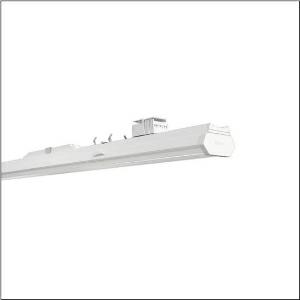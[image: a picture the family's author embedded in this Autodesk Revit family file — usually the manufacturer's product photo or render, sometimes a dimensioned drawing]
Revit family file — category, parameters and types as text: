
# Revit family: licross_r__11_protected_extreme_mo_51tp12dn495ge_fe34
name_source: partatom
category: Lighting Fixtures
units: mm (PartAtom-declared; Revit-internal decimal feet)

## family parameters
Cut with Voids When Loaded = No
Host = Face
Light Source = No
Part Type = Normal
Room Calculation Point = No
Round Connector Dimension = Use Diameter
Shared = No

## types (1)
- --- (1 x LED, 9980 lm, 57.1 W, 4000K)
    Apparent Load = 57 VA
    CIE Flux Codes = 73 92 98 99 100
    Color Rendering = 80
    Color Temperature = 4000K
    Default Elevation = 1800 mm
    Description = Licross® 11 Protected extreme MO, luminaire insert, of sheet steel, galvanised, coil coated, white, length: 1.500mm, width: 90mm, height: 101mm, LED rated luminous flux: 9.980lm, light colour: 840, control gear: DALI 2, with plug, 5-pole, with phase selection, mains connection: 220..240V, AC, 50/60Hz, rated input power: 57W, halogen-free wiring, primary optical cover: cover, of PMMA, light emission: direct distribution, primary light characteristic: symmetric, protection rating (complete): IP64, insulation class (complete): insulation class I (protective earthing), certification: CE, ENEC, VDE, UKCA, protection symbol: D if used in an environment with conductive dust loads with corresponding accessories, impact resistance: IK06, permissible ambient temperature for indoor applications: -40..+45°C, corresponds to IFS (International Featured Standards) requirements for safety and quality in the food industry, reducing of maximum allowable ambient temperature of 5°C with ceiling mounting, LABS conformity tested according to VDMA 24364:2018-05, packaging unit: 1 piece
    Height = 92 mm
    Lamp = 1 x LED
    Lamp Light Flux = 9980 lm
    Lamp Power = 57.1 W
    Lamp count = 1
    Length = 1500 mm
    Luminous efficacy = 175 lm/W
    Manufacturer = Siteco
    ModVariant = No
    Model = 51TP12DN495GE
    Mounting Place = Ceiling
    Mounting Type = Pendant
    Number of Poles = 1
    OnlyDefault = Yes
    Power Factor = 1
    Product Name = Licross® 11 Protected extreme MO
    Product group = luminaire insert
    ProductGroupID = 902
    Protection Class = Protection class I
    Protection Degree = IP 64
    RLX_Detail_Level = 1
    RLX_Emergency_Light_Flux = 0 lm
    RLX_Emergency_Type = 0
    RLX_Emergency_Type_DB = No
    RlxData = <blob elided: 24481 chars, md5=b0566ea1>
    Socket = socket
    Standby Power = 0 W
    System Light Flux = 9980 lm
    System Power = 57 W
    Type Comments = factory setting: luminous flux: 100 % | dim-lin: 254 | 378 mA
    Type Image = l_1256148.jpg
    URL = http://relux.com
    VarID = @adj_082658
    Voltage = 0 V
    Weight = 0.00 kg
    Width = 88 mm

## geometry (parser evidence)
native form markers: Blend x4, Sweep x12
no freeform markers — native parametric forms only
